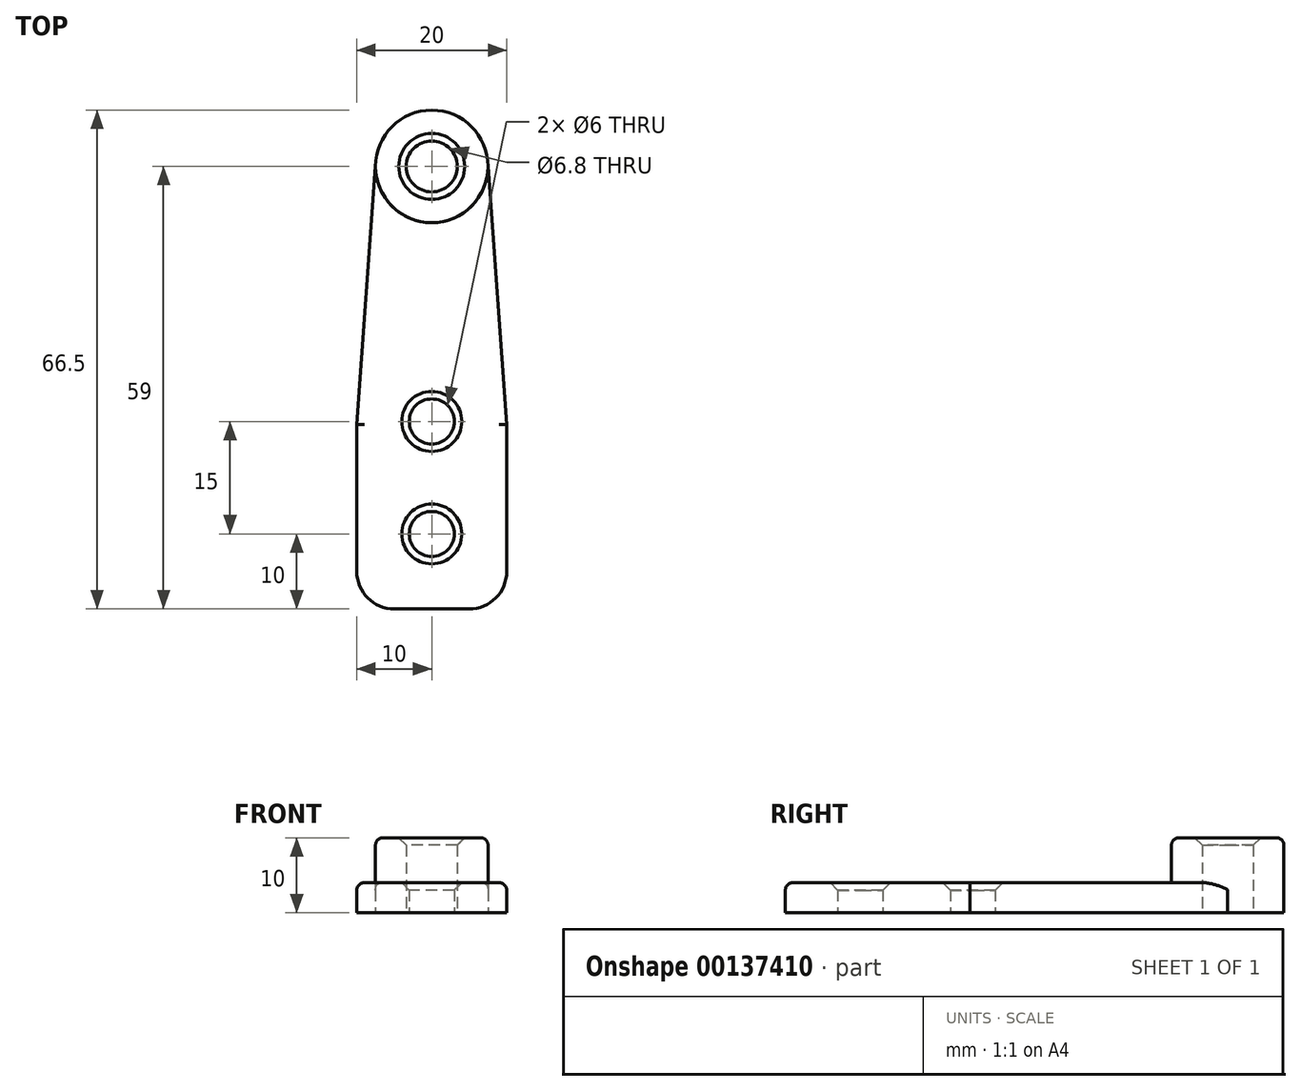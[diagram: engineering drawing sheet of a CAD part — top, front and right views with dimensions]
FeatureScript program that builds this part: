
annotation { "Feature Type Name" : "Feature", "Feature Type Description" : "" }
export const myFeature = defineFeature(function(context is Context, id is Id, definition is map)
    precondition{}
    {
        {
            var Q0;
            Q0=qCreatedBy(makeId("Top.planeOp"),FACE);
            var sketch = newSketch(context, id + "F0", { "sketchPlane" : qUnion([Q0])});
            skCircle(sketch, "E0", {"center": v(0, 0) * mm, "radius": 7.5 * mm});
            skLineSegment(sketch, "E1", {"start": v(-7.5, -72.35) * mm, "end": v(6.57, -72.35) * mm});
            skLineSegment(sketch, "E2", {"start": v(-10, -34.39) * mm, "end": v(-7.5, 0) * mm});
            skLineSegment(sketch, "E3", {"start": v(7.5, 0) * mm, "end": v(10, -34.39) * mm});
            skCircle(sketch, "E4", {"center": v(0, 0) * mm, "radius": 3.4 * mm});
            skCircle(sketch, "E5", {"center": v(0, -34) * mm, "radius": 3 * mm});
            skLineSegment(sketch, "E6.left", {"start": v(-10, -34.39) * mm, "end": v(-10, -34.39) * mm});
            skLineSegment(sketch, "E7", {"start": v(-10, -34.39) * mm, "end": v(-10, -54) * mm});
            skLineSegment(sketch, "E8", {"start": v(-5, -59) * mm, "end": v(5, -59) * mm});
            skLineSegment(sketch, "E9", {"start": v(10, -34.39) * mm, "end": v(10, -54) * mm});
            skPoint(sketch, "E10.visualSharp", {"position": v(-10, -59) * mm});
            skArc(sketch, "E10.filletArc", {"start": v(-10, -54) * mm, "mid": v(-8.54, -57.54) * mm, "end": v(-5, -59) * mm});
            skPoint(sketch, "E11.visualSharp", {"position": v(10, -59) * mm});
            skArc(sketch, "E11.filletArc", {"start": v(5, -59) * mm, "mid": v(8.54, -57.54) * mm, "end": v(10, -54) * mm});
            skCircle(sketch, "E12", {"center": v(0, -49) * mm, "radius": 3 * mm});
            skSolve(sketch);
        }
        {
            var Q0;
            {var subQ1=sQuery(id+"F0.wireOp",EDGE,"E2");Q0=makeQuery(id+"F0.imprint","IMPRINT",FACE,{"disambiguationData":[TD([[makeQuery(id+"F0.imprint","IMPRINT",EDGE,{"derivedFrom":subQ1}),-1.0]])]});}
            extrude(context, id + "F1", {"entities" : qUnion([Q0]), "depth" : 4 * mm});
        }
        {
            var Q0;
            Q0=makeQuery(id+"F0.imprint","IMPRINT",FACE,{"disambiguationData":[TD([[makeQuery(id+"F0.imprint","IMPRINT",EDGE,{"derivedFrom":sQuery(id+"F0.wireOp",EDGE,"E4")}),-1.0]])]});
            extrude(context, id + "F2", {"entities" : qUnion([Q0]), "operationType" : NewBodyOperationType.ADD, "depth" : 10 * mm});
        }
        {
            var Q0;
            Q0=makeQuery(id+"F1.opExtrude","CAP_EDGE",EDGE,{"disambiguationData":[OSD([sQuery(id+"F0.wireOp",EDGE,"E5")])],"isStart":false});
            var Q1;
            Q1=makeQuery(id+"F1.opExtrude","CAP_EDGE",EDGE,{"disambiguationData":[OSD([sQuery(id+"F0.wireOp",EDGE,"E12")])],"isStart":false});
            var Q2;
            Q2=makeQuery(id+"F2.opExtrude","CAP_EDGE",EDGE,{"disambiguationData":[OSD([sQuery(id+"F0.wireOp",EDGE,"E4")])],"isStart":false});
            chamfer(context, id + "F3", {"entities" : qUnion([Q0, Q1, Q2]), "width" : 1 * mm, "tangentPropagation" : true});
        }
        {
            var Q0;
            Q0=makeQuery(id+"F2.opExtrude","CAP_EDGE",EDGE,{"disambiguationData":[OSD([sQuery(id+"F0.wireOp",EDGE,"E0")])],"isStart":false});
            var Q1;
            Q1=makeQuery(id+"F1.opExtrude","CAP_EDGE",EDGE,{"disambiguationData":[OSD([sQuery(id+"F0.wireOp",EDGE,"E2")])],"isStart":false});
            var Q2;
            Q2=makeQuery(id+"F1.opExtrude","CAP_EDGE",EDGE,{"disambiguationData":[OSD([sQuery(id+"F0.wireOp",EDGE,"E7")])],"isStart":false});
            var Q3;
            Q3=makeQuery(id+"F1.opExtrude","CAP_EDGE",EDGE,{"disambiguationData":[OSD([sQuery(id+"F0.wireOp",EDGE,"E10.filletArc")])],"isStart":false});
            var Q4;
            Q4=makeQuery(id+"F1.opExtrude","CAP_EDGE",EDGE,{"disambiguationData":[OSD([sQuery(id+"F0.wireOp",EDGE,"E3")])],"isStart":false});
            fillet(context, id + "F4", {"entities" : qUnion([Q0, Q1, Q2, Q3, Q4]), "radius" : 1 * mm, "tangentPropagation" : true, "allowEdgeOverflow" : false});
        }
    });
